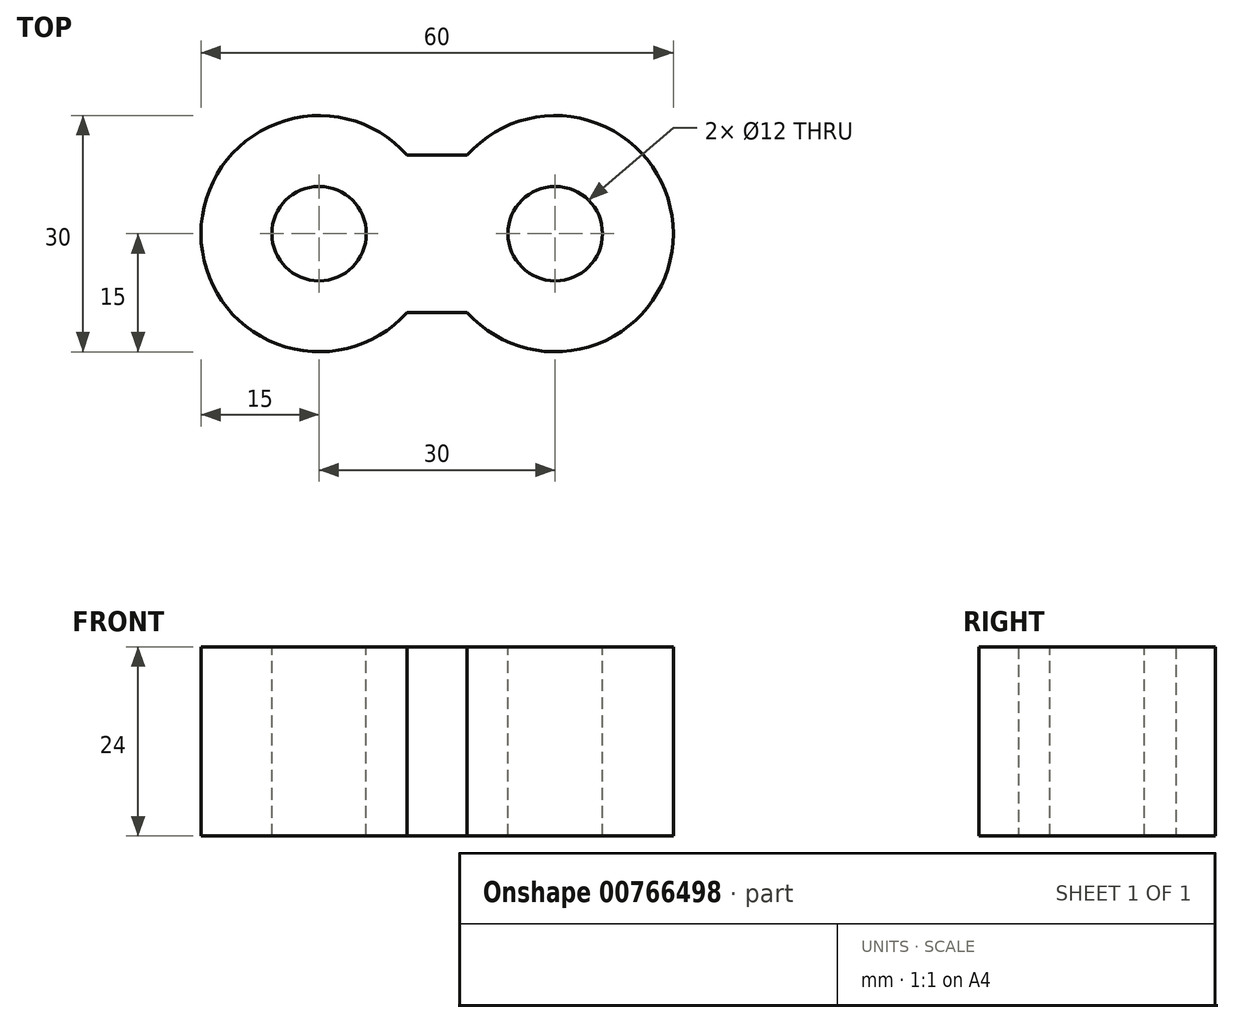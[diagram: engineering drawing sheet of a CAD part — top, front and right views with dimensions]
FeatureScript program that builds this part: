
annotation { "Feature Type Name" : "Feature", "Feature Type Description" : "" }
export const myFeature = defineFeature(function(context is Context, id is Id, definition is map)
    precondition{}
    {
        {
            var Q0;
            Q0=qCreatedBy(makeId("Top.planeOp"),FACE);
            var sketch = newSketch(context, id + "F0", { "sketchPlane" : qUnion([Q0])});
            skPoint(sketch, "E0", {"position": v(-15, 0) * mm});
            skPoint(sketch, "E1", {"position": v(15, 0) * mm});
            skCircle(sketch, "E2", {"center": v(-15, 0) * mm, "radius": 15 * mm});
            skCircle(sketch, "E3", {"center": v(15, 0) * mm, "radius": 15 * mm});
            skPoint(sketch, "E4", {"position": v(0, 10) * mm});
            skPoint(sketch, "E5", {"position": v(0, -10) * mm});
            skLineSegment(sketch, "E6", {"start": v(3.82, 10) * mm, "end": v(-3.82, 10) * mm});
            skLineSegment(sketch, "E7", {"start": v(0, -10) * mm, "end": v(3.82, -10) * mm});
            skLineSegment(sketch, "E8", {"start": v(3.82, -10) * mm, "end": v(-3.82, -10) * mm});
            skSolve(sketch);
        }
        {
            var Q0;
            Q0=qSketchRegion(id+"F0",true);
            extrude(context, id + "F1", {"entities" : qUnion([Q0]), "depth" : 24 * mm, "offsetDistance" : 25 * mm});
        }
        {
            var Q0;
            Q0=makeQuery(id+"F1.opExtrude","CAP_FACE",FACE,{"disambiguationData":[OSD([sQuery(id+"F0.wireOp",EDGE,"E2"),sQuery(id+"F0.wireOp",EDGE,"E3"),sQuery(id+"F0.wireOp",EDGE,"E6"),sQuery(id+"F0.wireOp",EDGE,"E8")])],"isStart":false});
            var sketch = newSketch(context, id + "F2", { "sketchPlane" : qUnion([Q0])});
            skPoint(sketch, "E9", {"position": v(-15, 0) * mm});
            skPoint(sketch, "E10", {"position": v(15, 0) * mm});
            skCircle(sketch, "E11", {"center": v(-15, 0) * mm, "radius": 6 * mm});
            skCircle(sketch, "E12", {"center": v(15, 0) * mm, "radius": 6 * mm});
            skSolve(sketch);
        }
        {
            var Q0;
            Q0=qSketchRegion(id+"F2",true);
            extrude(context, id + "F3", {"entities" : qUnion([Q0]), "operationType" : NewBodyOperationType.REMOVE, "endBound" : BoundingType.THROUGH_ALL, "oppositeDirection" : true, "depth" : 25 * mm, "offsetDistance" : 25 * mm});
        }
    });
